# Revit family: Table-Multi_Level_Workstations-BM_R_Fixed_Run_Off_Mid_Height_Kneespace_Module-R2018
name_source: partatom
category: Furniture
revit_build: Autodesk Revit 2018 (Build: 20190510_1515(x64)
units: mm (PartAtom-declared; Revit-internal decimal feet)

## family parameters
Always vertical = Yes
Cut with Voids When Loaded = No
OmniClass Number = 23.40.20.00
OmniClass Title = General Furniture and Specialties
Room Calculation Point = No
Shared = Yes
Work Plane-Based = No

## types (7) — shared parameters
Assembly Code = E2020200
Manufacturer = Teknion
Manufacturer Fax = 416.661.4586
Part Number = BM_R
Product Documentation Link = https://www.teknion.com
Product Documentation Link #10 = https://www.teknion.com
Product Documentation Link #2 = https://www.teknion.com
Product Documentation Link #3 = https://www.teknion.com
Product Documentation Link #4 = https://www.teknion.com
Product Documentation Link #5 = https://www.teknion.com
Product Documentation Link #6 = https://www.teknion.com
Product Documentation Link #7 = https://www.teknion.com
Product Documentation Link #8 = https://www.teknion.com
Product Documentation Link #9 = https://www.teknion.com
Product Line = Expansion Casegoods
Product Page URL = https://www.teknion.com
Series = Expansion Casegoods
Sustainability Data = https://www.teknion.com
URL = www.teknion.com
Unit Weight URL = http://www.teknion.com
Warranty = http://www.teknion.com

## per-type parameters (varying)
| type | Blade Leg | Description | Model | Semi-Supported Leg |
| Bevel Base | No | Fixed Run-Off for Mid-Height Kneespace Module, Mid-Height Configuration, Straight Corner Detail, Bevel Base | BM_RK__S__B | No |
| Semi-Supported leg | No | Fixed Run-Off for Mid-Height Kneespace Module, Mid-Height Configuration, Straight Corner Detail, Semi-Supported Leg | BM_RK__S__E | Yes |
| Blade Leg | Yes | Fixed Run-Off for Mid-Height Kneespace Module, Mid-Height Configuration, Blade Leg | BM_RK_____K | No |
| Fixed Bevel Post Leg | No | Fixed Run-Off for Mid-Height Kneespace Module, Mid-Height Configuration, Fixed Bevel Post Leg | BM_RK_____L | No |
| Frame Leg - Open | No | Fixed Run-Off for Mid-Height Kneespace Module, Mid-Height Configuration, Straight Corner Detail, Frame Leg - Open End Panel | BM_RK__S__W | No |
| Frame Leg - Solid Infill End Panel | No | Fixed Run-Off for Mid-Height Kneespace Module, Mid-Height Configuration, Straight Corner Detail, Frame Leg - Solid Infill End Panel | BM_RK__S__W | No |
| Frame Leg - Glass Infill End Panel | No | Fixed Run-Off for Mid-Height Kneespace Module, Mid-Height Configuration, Straight Corner Detail, Frame Leg - Glass Infill End Panel | BM_RK__S__W | No |

type visibility flags (boolean, named after types; folded from table):
- Bevel Base: Yes: Bevel Base
- Semi-Supported leg: Yes: (none)
- Blade Leg: Yes: (none)
- Fixed Bevel Post Leg: Yes: Fixed Bevel Post Leg
- Frame Leg - Open: Yes: Frame Leg - Open
- Frame Leg - Solid Infill End Panel: Yes: Frame Leg - Solid Infill End Panel
- Frame Leg - Glass Infill End Panel: Yes: Frame Leg - Glass Infill End Panel

## geometry (parser evidence)
native form markers: Blend x2, Sweep x5
no freeform markers — native parametric forms only
